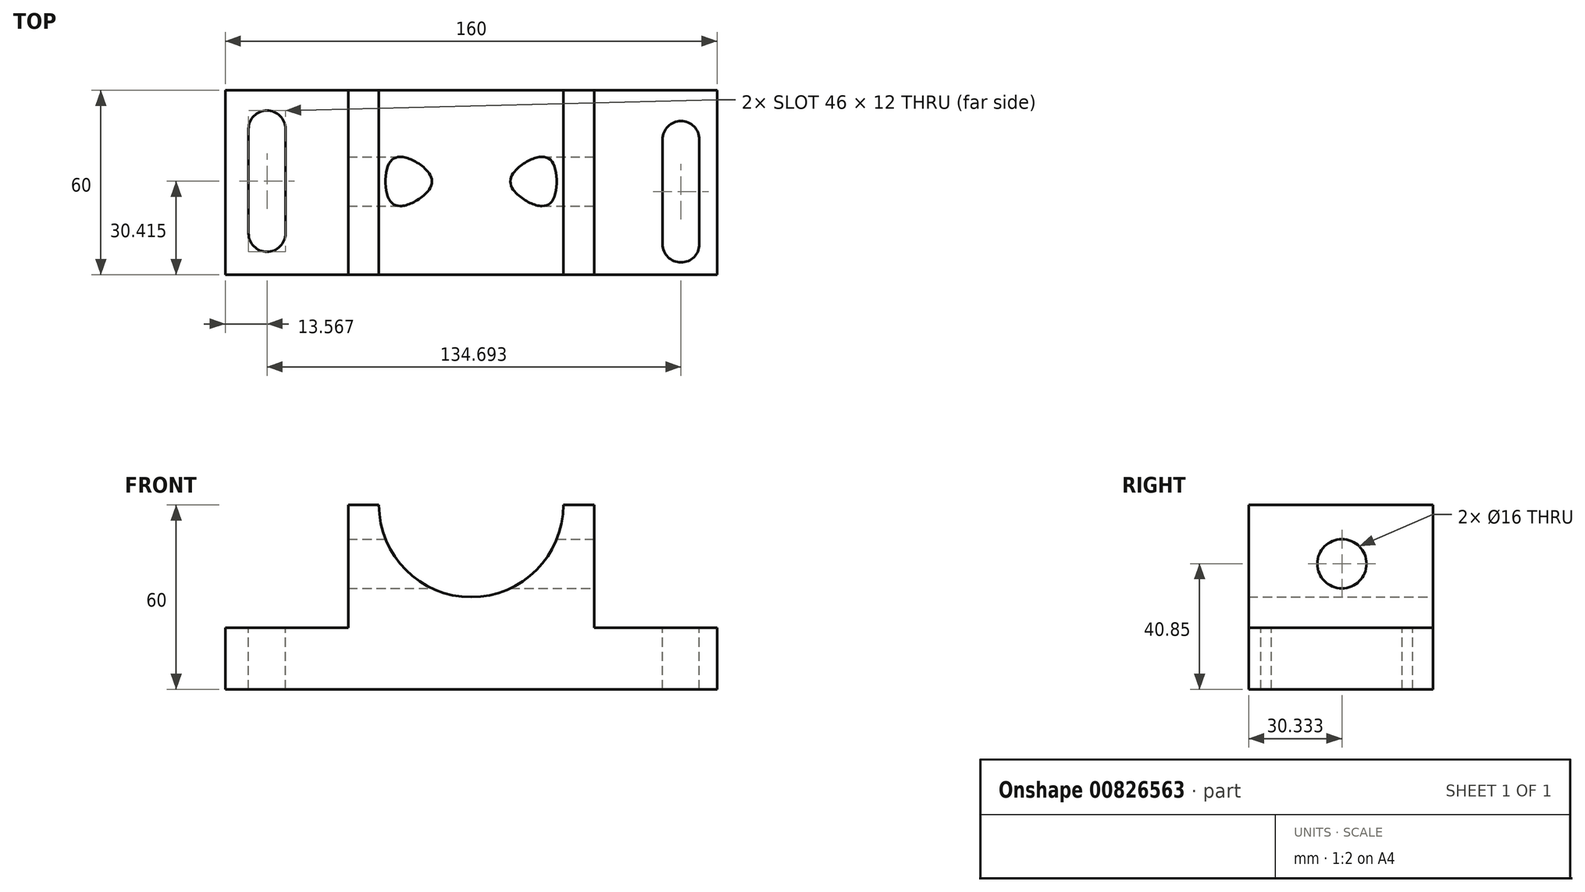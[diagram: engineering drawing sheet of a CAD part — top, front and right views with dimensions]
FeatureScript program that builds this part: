
annotation { "Feature Type Name" : "Feature", "Feature Type Description" : "" }
export const myFeature = defineFeature(function(context is Context, id is Id, definition is map)
    precondition{}
    {
        {
            var Q0;
            Q0=qCreatedBy(makeId("Front.planeOp"),FACE);
            var sketch = newSketch(context, id + "F0", { "sketchPlane" : qUnion([Q0])});
            skLineSegment(sketch, "E0.bottom", {"start": v(-80, -28.38) * mm, "end": v(80, -28.38) * mm});
            skLineSegment(sketch, "E0.top", {"start": v(-80, -48.38) * mm, "end": v(80, -48.38) * mm});
            skLineSegment(sketch, "E0.left", {"start": v(-80, -28.38) * mm, "end": v(-80, -48.38) * mm});
            skLineSegment(sketch, "E0.right", {"start": v(80, -28.38) * mm, "end": v(80, -48.38) * mm});
            skLineSegment(sketch, "E1", {"start": v(-80, -28.38) * mm, "end": v(0, -28.38) * mm});
            skLineSegment(sketch, "E2", {"start": v(0, -28.38) * mm, "end": v(0, -18.38) * mm});
            skLineSegment(sketch, "E3", {"start": v(30, 11.62) * mm, "end": v(40, 11.62) * mm});
            skLineSegment(sketch, "E4", {"start": v(-30, 11.62) * mm, "end": v(-40, 11.62) * mm});
            skLineSegment(sketch, "E5", {"start": v(40, 11.62) * mm, "end": v(40, -28.38) * mm});
            skLineSegment(sketch, "E6", {"start": v(-40, 11.62) * mm, "end": v(-40, -28.38) * mm});
            skArc(sketch, "E7", {"start": v(-30, 11.62) * mm, "mid": v(0, -18.38) * mm, "end": v(30, 11.62) * mm});
            skSolve(sketch);
        }
        {
            var Q0;
            {var subQ1=sQuery(id+"F0.wireOp",EDGE,"E2");var subQ2=makeQuery(id+"F0.imprint","IMPRINT",EDGE,{"derivedFrom":subQ1});Q0=qUnion([makeQuery(id+"F0.imprint","IMPRINT",FACE,{"disambiguationData":[TD([[makeQuery(id+"F0.imprint","IMPRINT",EDGE,{"derivedFrom":sQuery(id+"F0.wireOp",EDGE,"E0.top")}),1.0]])]}),makeQuery(id+"F0.imprint","IMPRINT",FACE,{"disambiguationData":[TD([[subQ2,1.0]])]}),makeQuery(id+"F0.imprint","IMPRINT",FACE,{"disambiguationData":[TD([[subQ2,-1.0]])]})]);}
            extrude(context, id + "F1", {"entities" : qUnion([Q0]), "depth" : 60 * mm, "offsetDistance" : 25 * mm});
        }
        {
            var Q0;
            {var subQ0=sQuery(id+"F0.wireOp",EDGE,"E0.bottom");Q0=makeQuery(id+"F1.opExtrude","SWEPT_FACE",FACE,{"disambiguationData":[OSD([subQ0]),TDD([makeQuery(id+"F0.imprint","IMPRINT",EDGE,{"disambiguationData":[TD([[makeQuery(id+"F0.imprint","INTERSECT",VERTEX,{"derivedFrom":[subQ0,sQuery(id+"F0.wireOp",EDGE,"E5")]}),-1.0]])],"derivedFrom":subQ0})])]});}
            var sketch = newSketch(context, id + "F2", { "sketchPlane" : qUnion([Q0])});
            skLineSegment(sketch, "E8", {"start": v(80, 0) * mm, "end": v(80, -30) * mm});
            skSolve(sketch);
        }
        {
            var Q0;
            {var subQ3=sQuery(id+"F2.wireOp",EDGE,"E8");Q0=makeQuery(id+"F2.imprint","IMPRINT",FACE,{"disambiguationData":[TD([[makeQuery(id+"F2.imprint","IMPRINT",EDGE,{"derivedFrom":subQ3}),1.0]])]});}
            var sketch = newSketch(context, id + "F3", { "sketchPlane" : qUnion([Q0])});
            skLineSegment(sketch, "E9.left", {"start": v(-72.43, -12.58) * mm, "end": v(-72.43, -46.58) * mm});
            skLineSegment(sketch, "E9.right", {"start": v(-60.43, -12.58) * mm, "end": v(-60.43, -46.58) * mm});
            skArc(sketch, "E10", {"start": v(-72.43, -12.58) * mm, "mid": v(-66.43, -6.58) * mm, "end": v(-60.43, -12.58) * mm});
            skArc(sketch, "E11", {"start": v(-72.43, -46.58) * mm, "mid": v(-66.43, -52.58) * mm, "end": v(-60.43, -46.58) * mm});
            skLineSegment(sketch, "E12.left", {"start": v(74.26, -50.03) * mm, "end": v(74.26, -16.03) * mm});
            skLineSegment(sketch, "E12.right", {"start": v(62.26, -50.03) * mm, "end": v(62.26, -16.03) * mm});
            skArc(sketch, "E13", {"start": v(62.26, -50.03) * mm, "mid": v(68.26, -56.03) * mm, "end": v(74.26, -50.03) * mm});
            skArc(sketch, "E14", {"start": v(62.26, -16.03) * mm, "mid": v(68.26, -10.03) * mm, "end": v(74.26, -16.03) * mm});
            skSolve(sketch);
        }
        {
            var Q0;
            Q0 = qSketchRegion(id + "F3", true);
            extrude(context, id + "F4", {"entities" : qUnion([Q0]), "operationType" : NewBodyOperationType.REMOVE, "endBound" : BoundingType.THROUGH_ALL, "oppositeDirection" : true, "depth" : 25 * mm, "offsetDistance" : 25 * mm});
        }
        {
            var Q0;
            Q0=makeQuery(id+"F1.opExtrude","SWEPT_FACE",FACE,{"disambiguationData":[OSD([sQuery(id+"F0.wireOp",EDGE,"E5")])]});
            var sketch = newSketch(context, id + "F5", { "sketchPlane" : qUnion([Q0])});
            skCircle(sketch, "E15", {"center": v(-29.67, -7.53) * mm, "radius": 8 * mm});
            skSolve(sketch);
        }
        {
            var Q0;
            Q0=makeQuery(id+"F5.imprint","IMPRINT",FACE,{"disambiguationData":[TD([[makeQuery(id+"F5.imprint","IMPRINT",EDGE,{"derivedFrom":sQuery(id+"F5.wireOp",EDGE,"E15")}),1.0]])]});
            extrude(context, id + "F6", {"entities" : qUnion([Q0]), "operationType" : NewBodyOperationType.REMOVE, "endBound" : BoundingType.THROUGH_ALL, "oppositeDirection" : true, "depth" : 25 * mm, "offsetDistance" : 25 * mm});
        }
    });
